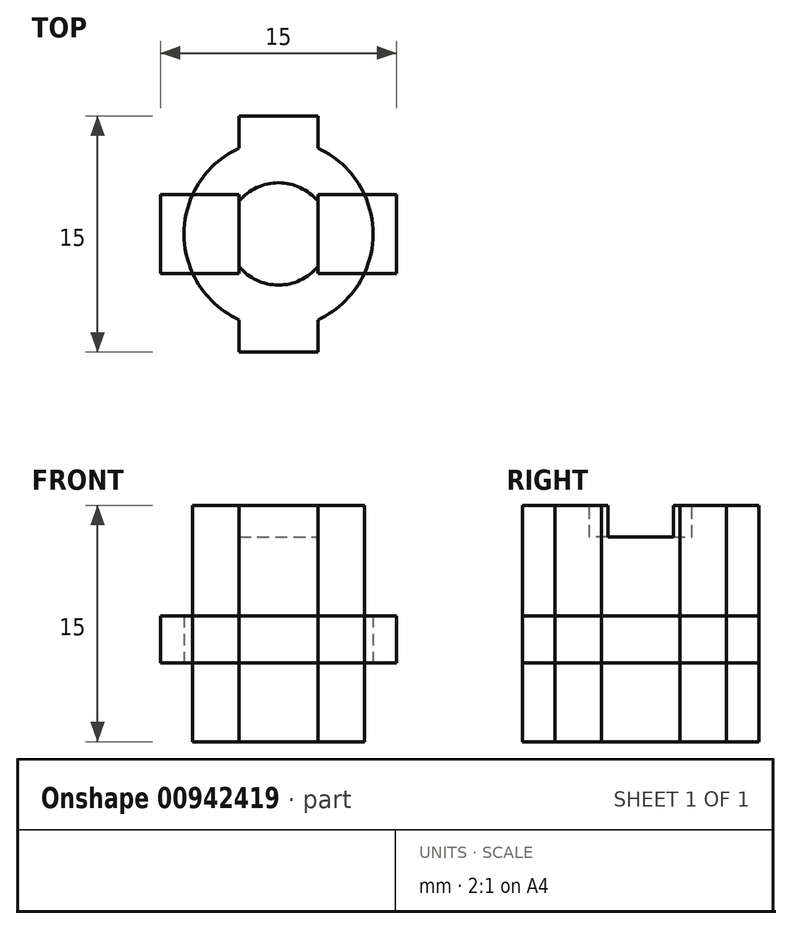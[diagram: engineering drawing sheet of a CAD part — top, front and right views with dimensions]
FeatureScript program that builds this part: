
annotation { "Feature Type Name" : "Feature", "Feature Type Description" : "" }
export const myFeature = defineFeature(function(context is Context, id is Id, definition is map)
    precondition{}
    {
        {
            var Q0;
            Q0=qCreatedBy(makeId("Top.planeOp"),FACE);
            var sketch = newSketch(context, id + "F0", { "sketchPlane" : qUnion([Q0])});
            skCircle(sketch, "E0.0", {"center": v(0, 0) * mm, "radius": 5.5 * mm, "construction": true});
            skCircle(sketch, "E1", {"center": v(0, 0) * mm, "radius": 6 * mm});
            skLineSegment(sketch, "E2", {"start": v(0, 13.29) * mm, "end": v(0, -11.87) * mm, "construction": true});
            skLineSegment(sketch, "E3", {"start": v(-2.5, 7.5) * mm, "end": v(2.5, 7.5) * mm});
            skLineSegment(sketch, "E4", {"start": v(2.5, 7.5) * mm, "end": v(2.5, -7.5) * mm});
            skLineSegment(sketch, "E5", {"start": v(2.5, -7.5) * mm, "end": v(-2.5, -7.5) * mm});
            skLineSegment(sketch, "E6", {"start": v(-2.5, -7.5) * mm, "end": v(-2.5, 7.5) * mm});
            skLineSegment(sketch, "E7", {"start": v(7.5, 2.5) * mm, "end": v(7.5, -2.5) * mm});
            skLineSegment(sketch, "E8", {"start": v(7.5, -2.5) * mm, "end": v(-7.5, -2.5) * mm});
            skLineSegment(sketch, "E9", {"start": v(-7.5, -2.5) * mm, "end": v(-7.5, 2.5) * mm});
            skLineSegment(sketch, "E10", {"start": v(-7.5, 2.5) * mm, "end": v(7.5, 2.5) * mm});
            skLineSegment(sketch, "E11", {"start": v(13.83, 0) * mm, "end": v(-10.1, 0) * mm, "construction": true});
            skSolve(sketch);
        }
        {
            var Q0;
            {var subQ0=sQuery(id+"F0.wireOp",EDGE,"E4");var subQ1=sQuery(id+"F0.wireOp",EDGE,"E1");var subQ2=makeQuery(id+"F0.imprint","INTERSECT",VERTEX,{"disambiguationData":[OD(0.0)],"derivedFrom":[subQ1,subQ0]});Q0=makeQuery(id+"F0.imprint","IMPRINT",FACE,{"disambiguationData":[TD([[makeQuery(id+"F0.imprint","IMPRINT",EDGE,{"disambiguationData":[TD([[subQ2,1.0]])],"derivedFrom":subQ1}),1.0]])]});}
            var Q1;
            {var subQ5=sQuery(id+"F0.wireOp",EDGE,"E5");Q1=makeQuery(id+"F0.imprint","IMPRINT",FACE,{"disambiguationData":[TD([[makeQuery(id+"F0.imprint","IMPRINT",EDGE,{"derivedFrom":subQ5}),-1.0]])]});}
            var Q2;
            {var subQ0=sQuery(id+"F0.wireOp",EDGE,"E8");var subQ1=sQuery(id+"F0.wireOp",EDGE,"E1");var subQ2=makeQuery(id+"F0.imprint","INTERSECT",VERTEX,{"disambiguationData":[OD(0.0)],"derivedFrom":[subQ1,subQ0]});Q2=makeQuery(id+"F0.imprint","IMPRINT",FACE,{"disambiguationData":[TD([[makeQuery(id+"F0.imprint","IMPRINT",EDGE,{"disambiguationData":[TD([[subQ2,-1.0]])],"derivedFrom":subQ1}),1.0]])]});}
            var Q3;
            {var subQ5=sQuery(id+"F0.wireOp",EDGE,"E9");Q3=makeQuery(id+"F0.imprint","IMPRINT",FACE,{"disambiguationData":[TD([[makeQuery(id+"F0.imprint","IMPRINT",EDGE,{"derivedFrom":subQ5}),-1.0]])]});}
            var Q4;
            {var subQ0=sQuery(id+"F0.wireOp",EDGE,"E4");var subQ1=sQuery(id+"F0.wireOp",EDGE,"E1");var subQ2=makeQuery(id+"F0.imprint","INTERSECT",VERTEX,{"disambiguationData":[OD(1.0)],"derivedFrom":[subQ1,subQ0]});Q4=makeQuery(id+"F0.imprint","IMPRINT",FACE,{"disambiguationData":[TD([[makeQuery(id+"F0.imprint","IMPRINT",EDGE,{"disambiguationData":[TD([[subQ2,-1.0]])],"derivedFrom":subQ1}),1.0]])]});}
            var Q5;
            {var subQ0=sQuery(id+"F0.wireOp",EDGE,"E6");var subQ1=sQuery(id+"F0.wireOp",EDGE,"E1");var subQ2=makeQuery(id+"F0.imprint","INTERSECT",VERTEX,{"disambiguationData":[OD(0.0)],"derivedFrom":[subQ1,subQ0]});Q5=makeQuery(id+"F0.imprint","IMPRINT",FACE,{"disambiguationData":[TD([[makeQuery(id+"F0.imprint","IMPRINT",EDGE,{"disambiguationData":[TD([[subQ2,-1.0]])],"derivedFrom":subQ1}),1.0]])]});}
            var Q6;
            {var subQ0=sQuery(id+"F0.wireOp",EDGE,"E10");var subQ1=sQuery(id+"F0.wireOp",EDGE,"E1");var subQ2=makeQuery(id+"F0.imprint","INTERSECT",VERTEX,{"disambiguationData":[OD(0.0)],"derivedFrom":[subQ1,subQ0]});Q6=makeQuery(id+"F0.imprint","IMPRINT",FACE,{"disambiguationData":[TD([[makeQuery(id+"F0.imprint","IMPRINT",EDGE,{"disambiguationData":[TD([[subQ2,1.0]])],"derivedFrom":subQ1}),1.0]])]});}
            var Q7;
            {var subQ0=sQuery(id+"F0.wireOp",EDGE,"E10");var subQ1=sQuery(id+"F0.wireOp",EDGE,"E4");var subQ2=makeQuery(id+"F0.imprint","INTERSECT",VERTEX,{"derivedFrom":[subQ1,subQ0]});Q7=makeQuery(id+"F0.imprint","IMPRINT",FACE,{"disambiguationData":[TD([[makeQuery(id+"F0.imprint","IMPRINT",EDGE,{"disambiguationData":[TD([[subQ2,-1.0]])],"derivedFrom":subQ1}),-1.0]])]});}
            var Q8;
            {var subQ0=sQuery(id+"F0.wireOp",EDGE,"E10");var subQ1=sQuery(id+"F0.wireOp",EDGE,"E1");var subQ2=makeQuery(id+"F0.imprint","INTERSECT",VERTEX,{"disambiguationData":[OD(1.0)],"derivedFrom":[subQ1,subQ0]});Q8=makeQuery(id+"F0.imprint","IMPRINT",FACE,{"disambiguationData":[TD([[makeQuery(id+"F0.imprint","IMPRINT",EDGE,{"disambiguationData":[TD([[subQ2,-1.0]])],"derivedFrom":subQ1}),1.0]])]});}
            var Q9;
            {var subQ0=sQuery(id+"F0.wireOp",EDGE,"E4");var subQ1=sQuery(id+"F0.wireOp",EDGE,"E1");var subQ2=makeQuery(id+"F0.imprint","INTERSECT",VERTEX,{"disambiguationData":[OD(0.0)],"derivedFrom":[subQ1,subQ0]});Q9=makeQuery(id+"F0.imprint","IMPRINT",FACE,{"disambiguationData":[TD([[makeQuery(id+"F0.imprint","IMPRINT",EDGE,{"disambiguationData":[TD([[subQ2,-1.0]])],"derivedFrom":subQ1}),1.0]])]});}
            var Q10;
            {var subQ5=sQuery(id+"F0.wireOp",EDGE,"E3");Q10=makeQuery(id+"F0.imprint","IMPRINT",FACE,{"disambiguationData":[TD([[makeQuery(id+"F0.imprint","IMPRINT",EDGE,{"derivedFrom":subQ5}),-1.0]])]});}
            var Q11;
            {var subQ5=sQuery(id+"F0.wireOp",EDGE,"E7");Q11=makeQuery(id+"F0.imprint","IMPRINT",FACE,{"disambiguationData":[TD([[makeQuery(id+"F0.imprint","IMPRINT",EDGE,{"derivedFrom":subQ5}),-1.0]])]});}
            var Q12;
            {var subQ0=sQuery(id+"F0.wireOp",EDGE,"E6");var subQ1=sQuery(id+"F0.wireOp",EDGE,"E1");var subQ2=makeQuery(id+"F0.imprint","INTERSECT",VERTEX,{"disambiguationData":[OD(1.0)],"derivedFrom":[subQ1,subQ0]});Q12=makeQuery(id+"F0.imprint","IMPRINT",FACE,{"disambiguationData":[TD([[makeQuery(id+"F0.imprint","IMPRINT",EDGE,{"disambiguationData":[TD([[subQ2,-1.0]])],"derivedFrom":subQ1}),1.0]])]});}
            extrude(context, id + "F1", {"entities" : qUnion([Q0, Q1, Q2, Q3, Q4, Q5, Q6, Q7, Q8, Q9, Q10, Q11, Q12]), "depth" : 3 * mm, "offsetDistance" : 25 * mm});
        }
        {
            var Q0;
            Q0=makeQuery(id+"F1.opExtrude","CAP_FACE",FACE,{"disambiguationData":[OSD([sQuery(id+"F0.wireOp",EDGE,"E1"),sQuery(id+"F0.wireOp",EDGE,"E3"),sQuery(id+"F0.wireOp",EDGE,"E4"),sQuery(id+"F0.wireOp",EDGE,"E5"),sQuery(id+"F0.wireOp",EDGE,"E6"),sQuery(id+"F0.wireOp",EDGE,"E7"),sQuery(id+"F0.wireOp",EDGE,"E8"),sQuery(id+"F0.wireOp",EDGE,"E9"),sQuery(id+"F0.wireOp",EDGE,"E10")])],"isStart":false});
            var sketch = newSketch(context, id + "F2", { "sketchPlane" : qUnion([Q0])});
            skLineSegment(sketch, "E12", {"start": v(0, 28.17) * mm, "end": v(0, 7.4) * mm, "construction": true});
            skPoint(sketch, "E12.startSnap0", {"position": v(0, 7.5) * mm});
            skPoint(sketch, "E12.endSnap0", {"position": v(0, -7.5) * mm});
            skLineSegment(sketch, "E13", {"start": v(-36.92, 0) * mm, "end": v(-18.15, 0) * mm, "construction": true});
            skPoint(sketch, "E13.startSnap0", {"position": v(-7.5, 0) * mm});
            skSolve(sketch);
        }
        {
            var Q0;
            Q0=qCreatedBy(makeId("Right.planeOp"),FACE);
            var sketch = newSketch(context, id + "F3", { "sketchPlane" : qUnion([Q0])});
            skArc(sketch, "E14", {"start": v(0, 0) * mm, "mid": v(-6, -6) * mm, "end": v(0, -12) * mm});
            skLineSegment(sketch, "E15", {"start": v(0, 0) * mm, "end": v(0, -12) * mm});
            skSolve(sketch);
        }
        {
            var Q0;
            Q0=makeQuery(id+"F3.imprint","IMPRINT",FACE,{"disambiguationData":[TD([[makeQuery(id+"F3.imprint","IMPRINT",EDGE,{"derivedFrom":sQuery(id+"F3.wireOp",EDGE,"E14")}),1.0]])]});
            var Q1;
            Q1=sQuery(id+"F3.wireOp",EDGE,"E15");
            revolve(context, id + "F4", {"surfaceOperationType" : NewSurfaceOperationType.NEW, "entities" : qUnion([Q0]), "axis" : qUnion([Q1]), "revolveType" : RevolveType.FULL});
        }
        {
            var Q0;
            Q0=makeQuery(id+"F1.opExtrude","CAP_FACE",FACE,{"disambiguationData":[OSD([sQuery(id+"F0.wireOp",EDGE,"E1"),sQuery(id+"F0.wireOp",EDGE,"E3"),sQuery(id+"F0.wireOp",EDGE,"E4"),sQuery(id+"F0.wireOp",EDGE,"E5"),sQuery(id+"F0.wireOp",EDGE,"E6"),sQuery(id+"F0.wireOp",EDGE,"E7"),sQuery(id+"F0.wireOp",EDGE,"E8"),sQuery(id+"F0.wireOp",EDGE,"E9"),sQuery(id+"F0.wireOp",EDGE,"E10")])],"isStart":true});
            extrude(context, id + "F5", {"entities" : qUnion([Q0]), "depth" : 5 * mm, "offsetDistance" : 25 * mm});
        }
        {
            var Q0;
            Q0=makeQuery(id+"F4.opRevolve","SWEPT_BODY",BODY,{"disambiguationData":[OSD([sQuery(id+"F3.wireOp",EDGE,"E14"),sQuery(id+"F3.wireOp",EDGE,"E15")])]});
            var Q1;
            Q1=makeQuery(id+"F1.opExtrude","SWEPT_BODY",BODY,{"disambiguationData":[OSD([sQuery(id+"F0.wireOp",EDGE,"E1"),sQuery(id+"F0.wireOp",EDGE,"E3"),sQuery(id+"F0.wireOp",EDGE,"E4"),sQuery(id+"F0.wireOp",EDGE,"E5"),sQuery(id+"F0.wireOp",EDGE,"E6"),sQuery(id+"F0.wireOp",EDGE,"E7"),sQuery(id+"F0.wireOp",EDGE,"E8"),sQuery(id+"F0.wireOp",EDGE,"E9"),sQuery(id+"F0.wireOp",EDGE,"E10")])]});
            booleanBodies(context, id + "F6", {"operationType" : BooleanOperationType.SUBTRACTION, "tools" : qUnion([Q0]), "targets" : qUnion([Q1])});
        }
        {
            var Q0;
            {var subQ1=sQuery(id+"F0.wireOp",EDGE,"E3");Q0=makeQuery(id+"F2.imprint","IMPRINT",FACE,{"disambiguationData":[TD([[makeQuery(id+"F2.imprint","IMPRINT",EDGE,{"derivedFrom":makeQuery(id+"F1.opExtrude","CAP_EDGE",EDGE,{"disambiguationData":[OSD([subQ1])],"isStart":false})}),-1.0]])]});}
            extrude(context, id + "F7", {"entities" : qUnion([Q0]), "depth" : 7 * mm, "offsetDistance" : 25 * mm});
        }
        {
            var Q0;
            Q0=makeQuery(id+"F7.opExtrude","CAP_FACE",FACE,{"disambiguationData":[OSD([sQuery(id+"F0.wireOp",EDGE,"E1"),sQuery(id+"F0.wireOp",EDGE,"E3"),sQuery(id+"F0.wireOp",EDGE,"E4"),sQuery(id+"F0.wireOp",EDGE,"E5"),sQuery(id+"F0.wireOp",EDGE,"E6"),sQuery(id+"F0.wireOp",EDGE,"E7"),sQuery(id+"F0.wireOp",EDGE,"E8"),sQuery(id+"F0.wireOp",EDGE,"E9"),sQuery(id+"F0.wireOp",EDGE,"E10")])],"isStart":false});
            var sketch = newSketch(context, id + "F8", { "sketchPlane" : qUnion([Q0])});
            skCircle(sketch, "E16", {"center": v(0, 0) * mm, "radius": 3.25 * mm});
            skSolve(sketch);
        }
        {
            var Q0;
            Q0=makeQuery(id+"F8.imprint","IMPRINT",FACE,{"disambiguationData":[TD([[makeQuery(id+"F8.imprint","IMPRINT",EDGE,{"derivedFrom":sQuery(id+"F8.wireOp",EDGE,"E16")}),1.0]])]});
            extrude(context, id + "F9", {"entities" : qUnion([Q0]), "operationType" : NewBodyOperationType.REMOVE, "oppositeDirection" : true, "depth" : 2 * mm, "offsetDistance" : 25 * mm});
        }
    });
